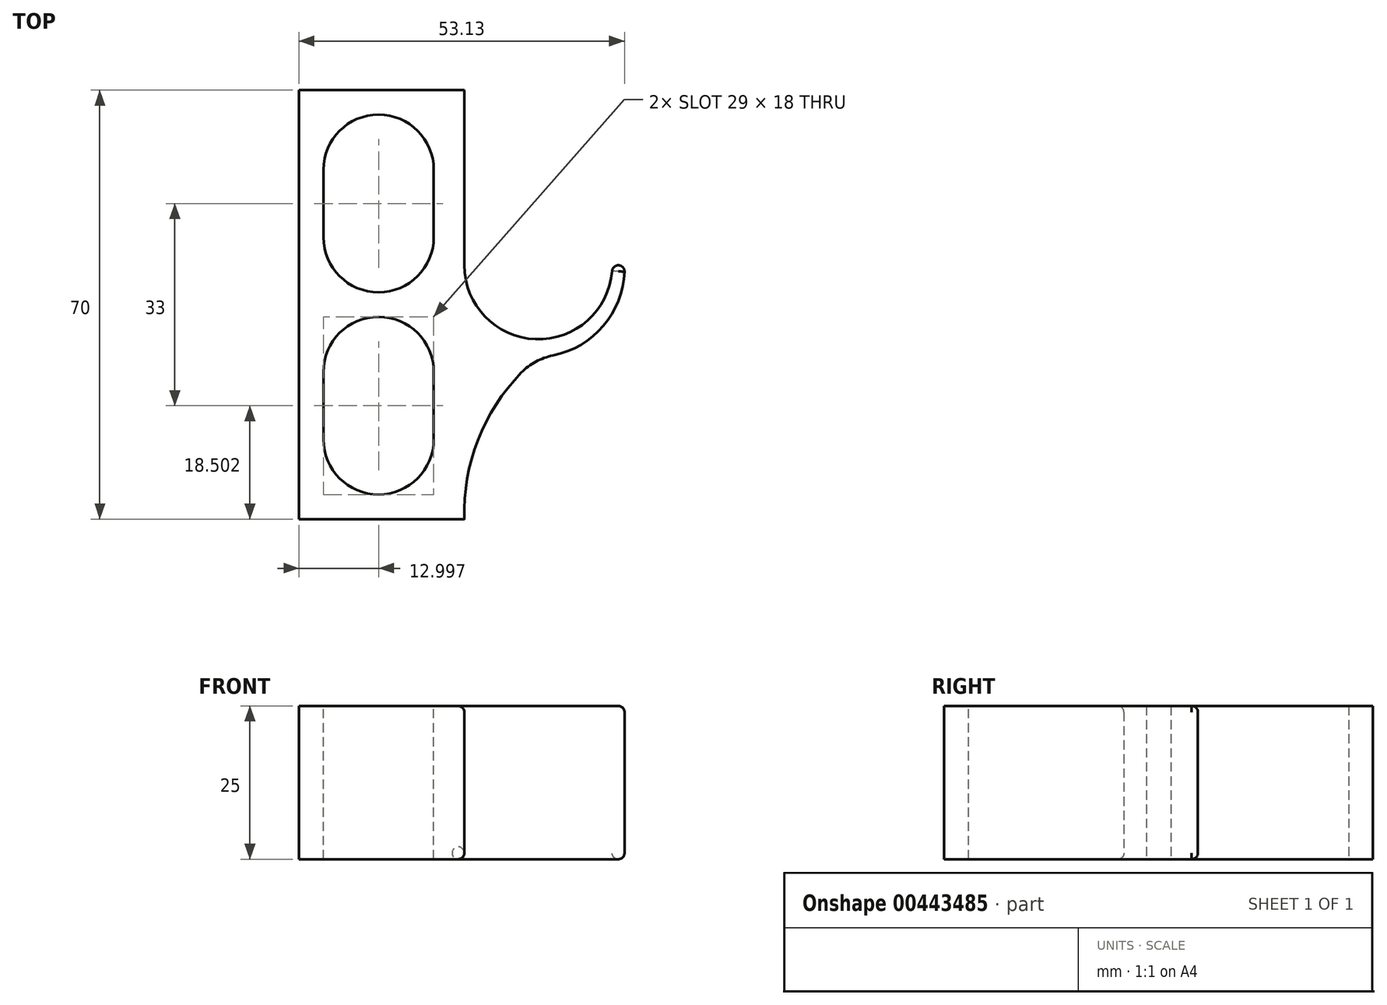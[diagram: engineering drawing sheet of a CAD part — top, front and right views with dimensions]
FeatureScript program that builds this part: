
annotation { "Feature Type Name" : "Feature", "Feature Type Description" : "" }
export const myFeature = defineFeature(function(context is Context, id is Id, definition is map)
    precondition{}
    {
        {
            var Q0;
            Q0=qCreatedBy(makeId("Top.planeOp"),FACE);
            var sketch = newSketch(context, id + "F0", { "sketchPlane" : qUnion([Q0])});
            skLineSegment(sketch, "E0", {"start": v(-22.35, 19.17) * mm, "end": v(-22.35, -50.83) * mm});
            skLineSegment(sketch, "E1", {"start": v(-22.35, -50.83) * mm, "end": v(-20.35, -50.83) * mm});
            skLineSegment(sketch, "E2", {"start": v(-22.35, 19.17) * mm, "end": v(-20.35, 19.17) * mm});
            skLineSegment(sketch, "E3", {"start": v(-20.35, 19.17) * mm, "end": v(-20.35, -9.42) * mm});
            skArc(sketch, "E4", {"start": v(-20.35, -9.42) * mm, "mid": v(-8.28, -21.49) * mm, "end": v(3.79, -9.42) * mm});
            skLineSegment(sketch, "E5", {"start": v(3.79, -9.42) * mm, "end": v(5.79, -9.42) * mm});
            skLineSegment(sketch, "E6", {"start": v(-8.28, -9.42) * mm, "end": v(-8.28, -55.65) * mm, "construction": true});
            skArc(sketch, "E7", {"start": v(-8.28, -24.4) * mm, "mid": v(1.86, -19.82) * mm, "end": v(5.79, -9.42) * mm});
            skArc(sketch, "E8", {"start": v(-8.28, -24.4) * mm, "mid": v(-17.42, -36.2) * mm, "end": v(-20.35, -50.83) * mm});
            skSolve(sketch);
        }
        {
            var Q0;
            Q0 = qSketchRegion(id + "F0", true);
            extrude(context, id + "F1", {"entities" : qUnion([Q0]), "depth" : 25 * mm});
        }
        {
            var Q0;
            Q0=makeQuery(id+"F1.opExtrude","SWEPT_EDGE",EDGE,{"disambiguationData":[OSD([sQuery(id+"F0.wireOp",EDGE,"E7"),sQuery(id+"F0.wireOp",EDGE,"E8")])]});
            fillet(context, id + "F2", {"entities" : qUnion([Q0]), "radius" : 10 * mm, "tangentPropagation" : true, "allowEdgeOverflow" : false});
        }
        {
            var Q0;
            Q0=makeQuery(id+"F1.opExtrude","CAP_EDGE",EDGE,{"disambiguationData":[OSD([sQuery(id+"F0.wireOp",EDGE,"E3")])],"isStart":false});
            var Q1;
            Q1=makeQuery(id+"F1.opExtrude","CAP_EDGE",EDGE,{"disambiguationData":[OSD([sQuery(id+"F0.wireOp",EDGE,"E4")])],"isStart":false});
            var Q2;
            Q2=makeQuery(id+"F1.opExtrude","CAP_EDGE",EDGE,{"disambiguationData":[OSD([sQuery(id+"F0.wireOp",EDGE,"E7")])],"isStart":false});
            var Q3;
            {var subQ0=sQuery(id+"F0.wireOp",EDGE,"E8");var subQ1=sQuery(id+"F0.wireOp",EDGE,"E7");Q3=makeQuery(id+"F2.opFillet","BLEND_EDGE",EDGE,{"blendedFrom":[makeQuery(id+"F1.opExtrude","SWEPT_EDGE",EDGE,{"disambiguationData":[OSD([subQ1,subQ0])]}),makeQuery(id+"F1.opExtrude","CAP_FACE",FACE,{"disambiguationData":[OSD([sQuery(id+"F0.wireOp",EDGE,"E0"),sQuery(id+"F0.wireOp",EDGE,"E1"),sQuery(id+"F0.wireOp",EDGE,"E2"),sQuery(id+"F0.wireOp",EDGE,"E3"),sQuery(id+"F0.wireOp",EDGE,"E4"),sQuery(id+"F0.wireOp",EDGE,"E5"),subQ1,subQ0])],"isStart":false})],"blendedInto":[makeQuery(id+"F1.opExtrude","CAP_FACE",FACE,{"disambiguationData":[OSD([sQuery(id+"F0.wireOp",EDGE,"E0"),sQuery(id+"F0.wireOp",EDGE,"E1"),sQuery(id+"F0.wireOp",EDGE,"E2"),sQuery(id+"F0.wireOp",EDGE,"E3"),sQuery(id+"F0.wireOp",EDGE,"E4"),sQuery(id+"F0.wireOp",EDGE,"E5"),subQ1,subQ0])],"isStart":false})]});}
            var Q4;
            Q4=makeQuery(id+"F1.opExtrude","CAP_EDGE",EDGE,{"disambiguationData":[OSD([sQuery(id+"F0.wireOp",EDGE,"E8")])],"isStart":false});
            var Q5;
            Q5=makeQuery(id+"F1.opExtrude","CAP_EDGE",EDGE,{"disambiguationData":[OSD([sQuery(id+"F0.wireOp",EDGE,"E4")])],"isStart":true});
            var Q6;
            {var subQ0=sQuery(id+"F0.wireOp",EDGE,"E8");var subQ1=sQuery(id+"F0.wireOp",EDGE,"E7");Q6=makeQuery(id+"F2.opFillet","BLEND_EDGE",EDGE,{"blendedFrom":[makeQuery(id+"F1.opExtrude","SWEPT_EDGE",EDGE,{"disambiguationData":[OSD([subQ1,subQ0])]}),makeQuery(id+"F1.opExtrude","CAP_FACE",FACE,{"disambiguationData":[OSD([sQuery(id+"F0.wireOp",EDGE,"E0"),sQuery(id+"F0.wireOp",EDGE,"E1"),sQuery(id+"F0.wireOp",EDGE,"E2"),sQuery(id+"F0.wireOp",EDGE,"E3"),sQuery(id+"F0.wireOp",EDGE,"E4"),sQuery(id+"F0.wireOp",EDGE,"E5"),subQ1,subQ0])],"isStart":true})],"blendedInto":[makeQuery(id+"F1.opExtrude","CAP_FACE",FACE,{"disambiguationData":[OSD([sQuery(id+"F0.wireOp",EDGE,"E0"),sQuery(id+"F0.wireOp",EDGE,"E1"),sQuery(id+"F0.wireOp",EDGE,"E2"),sQuery(id+"F0.wireOp",EDGE,"E3"),sQuery(id+"F0.wireOp",EDGE,"E4"),sQuery(id+"F0.wireOp",EDGE,"E5"),subQ1,subQ0])],"isStart":true})]});}
            fillet(context, id + "F3", {"entities" : qUnion([Q0, Q1, Q2, Q3, Q4, Q5, Q6]), "radius" : 1 * mm, "tangentPropagation" : true, "allowEdgeOverflow" : false});
        }
        {
            var Q0;
            Q0=makeQuery(id+"F1.opExtrude","SWEPT_EDGE",EDGE,{"disambiguationData":[OSD([sQuery(id+"F0.wireOp",EDGE,"E5"),sQuery(id+"F0.wireOp",EDGE,"E7")])]});
            var Q1;
            Q1=makeQuery(id+"F1.opExtrude","SWEPT_FACE",FACE,{"disambiguationData":[OSD([sQuery(id+"F0.wireOp",EDGE,"E5")])]});
            fillet(context, id + "F4", {"entities" : qUnion([Q0, Q1]), "radius" : 1 * mm, "tangentPropagation" : true, "allowEdgeOverflow" : false});
        }
        {
            var Q0;
            Q0=makeQuery(id+"F1.opExtrude","SWEPT_FACE",FACE,{"disambiguationData":[OSD([sQuery(id+"F0.wireOp",EDGE,"E0")])]});
            var sketch = newSketch(context, id + "F5", { "sketchPlane" : qUnion([Q0])});
            skLineSegment(sketch, "E9.bottom", {"start": v(-19.17, 0) * mm, "end": v(50.83, 0) * mm});
            skLineSegment(sketch, "E9.top", {"start": v(-19.17, 25) * mm, "end": v(50.83, 25) * mm});
            skLineSegment(sketch, "E9.left", {"start": v(-19.17, 0) * mm, "end": v(-19.17, 25) * mm});
            skLineSegment(sketch, "E9.right", {"start": v(50.83, 0) * mm, "end": v(50.83, 25) * mm});
            skSolve(sketch);
        }
        {
            var Q0;
            Q0 = qSketchRegion(id + "F5", true);
            extrude(context, id + "F6", {"entities" : qUnion([Q0]), "operationType" : NewBodyOperationType.ADD, "depth" : 25 * mm, "offsetDistance" : 25 * mm});
        }
        {
            var Q0;
            Q0=makeQuery(id+"F6.boolean.opBoolean","MERGE",FACE,{"derivedFrom":[makeQuery(id+"F1.opExtrude","CAP_FACE",FACE,{"disambiguationData":[OSD([sQuery(id+"F0.wireOp",EDGE,"E0"),sQuery(id+"F0.wireOp",EDGE,"E1"),sQuery(id+"F0.wireOp",EDGE,"E2"),sQuery(id+"F0.wireOp",EDGE,"E3"),sQuery(id+"F0.wireOp",EDGE,"E4"),sQuery(id+"F0.wireOp",EDGE,"E5"),sQuery(id+"F0.wireOp",EDGE,"E7"),sQuery(id+"F0.wireOp",EDGE,"E8")])],"isStart":false}),makeQuery(id+"F6.opExtrude","SWEPT_FACE",FACE,{"disambiguationData":[OSD([sQuery(id+"F5.wireOp",EDGE,"E9.top")])]})]});
            var sketch = newSketch(context, id + "F7", { "sketchPlane" : qUnion([Q0])});
            skLineSegment(sketch, "E10.bottom", {"start": v(-43.35, 15.17) * mm, "end": v(-25.35, 15.17) * mm});
            skLineSegment(sketch, "E10.top", {"start": v(-43.35, -13.83) * mm, "end": v(-25.35, -13.83) * mm});
            skLineSegment(sketch, "E10.left", {"start": v(-43.35, 15.17) * mm, "end": v(-43.35, -13.83) * mm});
            skLineSegment(sketch, "E10.right", {"start": v(-25.35, 15.17) * mm, "end": v(-25.35, -13.83) * mm});
            skLineSegment(sketch, "E11.bottom", {"start": v(-25.35, -17.83) * mm, "end": v(-43.35, -17.83) * mm});
            skLineSegment(sketch, "E11.top", {"start": v(-25.35, -46.83) * mm, "end": v(-43.35, -46.83) * mm});
            skLineSegment(sketch, "E11.left", {"start": v(-25.35, -17.83) * mm, "end": v(-25.35, -46.83) * mm});
            skLineSegment(sketch, "E11.right", {"start": v(-43.35, -17.83) * mm, "end": v(-43.35, -46.83) * mm});
            skSolve(sketch);
        }
        {
            var Q0;
            Q0 = qSketchRegion(id + "F7", true);
            extrude(context, id + "F8", {"entities" : qUnion([Q0]), "operationType" : NewBodyOperationType.REMOVE, "oppositeDirection" : true, "depth" : 25 * mm, "offsetDistance" : 25 * mm});
        }
        {
            var Q0;
            Q0=makeQuery(id+"F8.boolean.opBoolean","COPY",EDGE,{"derivedFrom":makeQuery(id+"F8.opExtrude","SWEPT_EDGE",EDGE,{"disambiguationData":[OSD([sQuery(id+"F7.wireOp",EDGE,"E10.bottom"),sQuery(id+"F7.wireOp",EDGE,"E10.right")])]})});
            var Q1;
            Q1=makeQuery(id+"F8.boolean.opBoolean","COPY",EDGE,{"derivedFrom":makeQuery(id+"F8.opExtrude","SWEPT_EDGE",EDGE,{"disambiguationData":[OSD([sQuery(id+"F7.wireOp",EDGE,"E10.bottom"),sQuery(id+"F7.wireOp",EDGE,"E10.left")])]})});
            var Q2;
            Q2=makeQuery(id+"F8.boolean.opBoolean","COPY",EDGE,{"derivedFrom":makeQuery(id+"F8.opExtrude","SWEPT_EDGE",EDGE,{"disambiguationData":[OSD([sQuery(id+"F7.wireOp",EDGE,"E11.bottom"),sQuery(id+"F7.wireOp",EDGE,"E11.right")])]})});
            var Q3;
            Q3=makeQuery(id+"F8.boolean.opBoolean","COPY",EDGE,{"derivedFrom":makeQuery(id+"F8.opExtrude","SWEPT_EDGE",EDGE,{"disambiguationData":[OSD([sQuery(id+"F7.wireOp",EDGE,"E11.bottom"),sQuery(id+"F7.wireOp",EDGE,"E11.left")])]})});
            var Q4;
            Q4=makeQuery(id+"F8.boolean.opBoolean","COPY",EDGE,{"derivedFrom":makeQuery(id+"F8.opExtrude","SWEPT_EDGE",EDGE,{"disambiguationData":[OSD([sQuery(id+"F7.wireOp",EDGE,"E10.top"),sQuery(id+"F7.wireOp",EDGE,"E10.left")])]})});
            var Q5;
            Q5=makeQuery(id+"F8.boolean.opBoolean","COPY",EDGE,{"derivedFrom":makeQuery(id+"F8.opExtrude","SWEPT_EDGE",EDGE,{"disambiguationData":[OSD([sQuery(id+"F7.wireOp",EDGE,"E11.top"),sQuery(id+"F7.wireOp",EDGE,"E11.right")])]})});
            var Q6;
            Q6=makeQuery(id+"F8.boolean.opBoolean","COPY",EDGE,{"derivedFrom":makeQuery(id+"F8.opExtrude","SWEPT_EDGE",EDGE,{"disambiguationData":[OSD([sQuery(id+"F7.wireOp",EDGE,"E10.top"),sQuery(id+"F7.wireOp",EDGE,"E10.right")])]})});
            var Q7;
            Q7=makeQuery(id+"F8.boolean.opBoolean","COPY",EDGE,{"derivedFrom":makeQuery(id+"F8.opExtrude","SWEPT_EDGE",EDGE,{"disambiguationData":[OSD([sQuery(id+"F7.wireOp",EDGE,"E11.top"),sQuery(id+"F7.wireOp",EDGE,"E11.left")])]})});
            fillet(context, id + "F9", {"entities" : qUnion([Q0, Q1, Q2, Q3, Q4, Q5, Q6, Q7]), "radius" : 9 * mm, "tangentPropagation" : true, "allowEdgeOverflow" : false});
        }
    });
